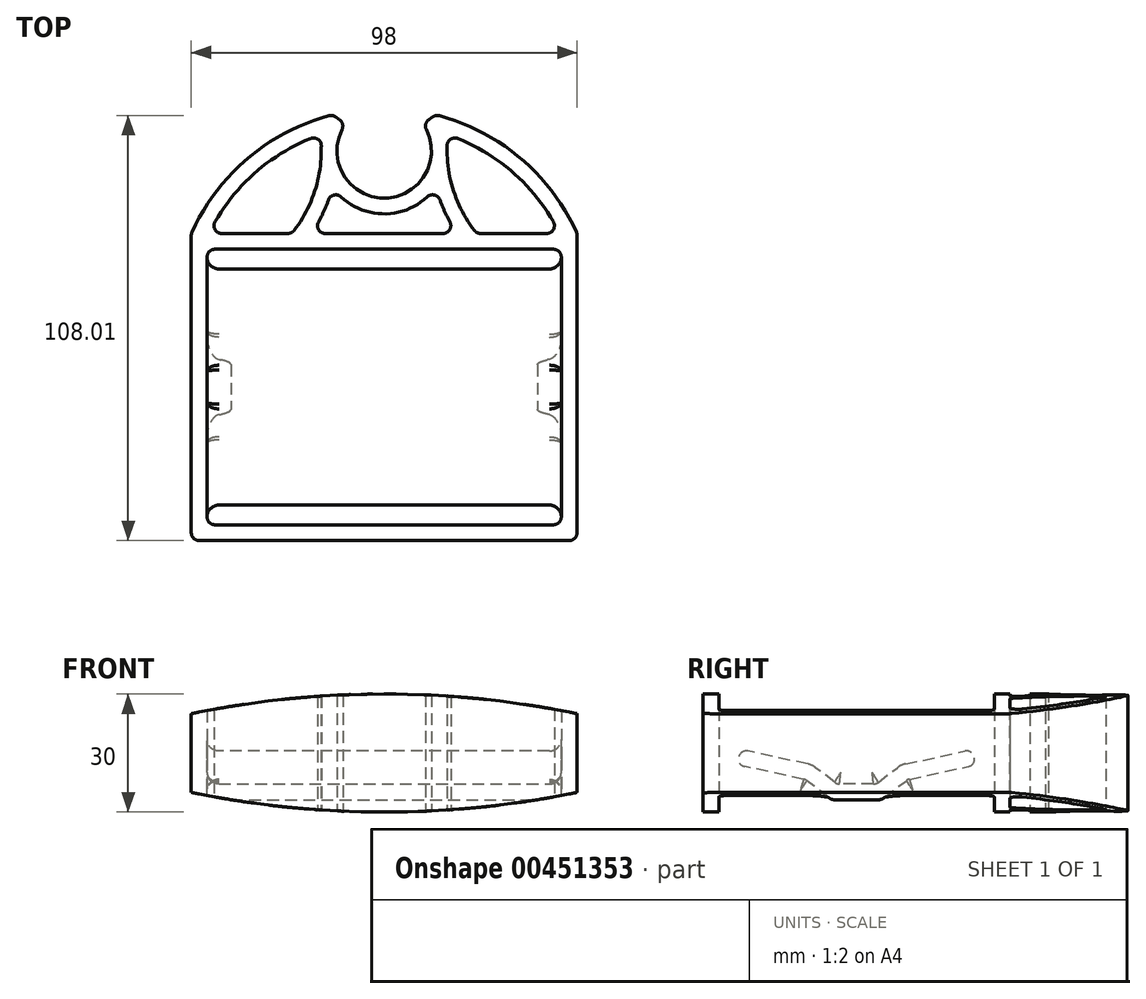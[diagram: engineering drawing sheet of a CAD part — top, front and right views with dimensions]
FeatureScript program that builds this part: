
annotation { "Feature Type Name" : "Feature", "Feature Type Description" : "" }
export const myFeature = defineFeature(function(context is Context, id is Id, definition is map)
    precondition{}
    {
        {
            var Q0;
            Q0=qCreatedBy(makeId("Top.planeOp"),FACE);
            var sketch = newSketch(context, id + "F0", { "sketchPlane" : qUnion([Q0])});
            skCircle(sketch, "E0", {"center": v(0, 0) * mm, "radius": 12 * mm});
            skSolve(sketch);
        }
        {
            var Q0;
            Q0=qCreatedBy(makeId("Top.planeOp"),FACE);
            var sketch = newSketch(context, id + "F1", { "sketchPlane" : qUnion([Q0])});
            skArc(sketch, "E1.0", {"start": v(-9.83, 6.88) * mm, "mid": v(-10.64, -5.54) * mm, "end": v(0, -12) * mm});
            skArc(sketch, "E2.0", {"start": v(-15.4, 4.36) * mm, "mid": v(-15.85, 2.2) * mm, "end": v(-16, 0) * mm});
            skLineSegment(sketch, "E3", {"start": v(0, -16) * mm, "end": v(0, -12) * mm});
            skLineSegment(sketch, "E4", {"start": v(0, 0) * mm, "end": v(0, -12) * mm, "construction": true});
            skPoint(sketch, "E5.orphan", {"position": v(0, 16) * mm});
            skLineSegment(sketch, "E6", {"start": v(-13.1, 9.18) * mm, "end": v(-9.83, 6.88) * mm});
            skLineSegment(sketch, "E7", {"start": v(0, 0) * mm, "end": v(-9.83, 6.88) * mm, "construction": true});
            skLineSegment(sketch, "E8", {"start": v(0, -16) * mm, "end": v(0, -21) * mm, "construction": true});
            skLineSegment(sketch, "E9", {"start": v(0, -21) * mm, "end": v(0, -25) * mm});
            skLineSegment(sketch, "E10", {"start": v(0, -21) * mm, "end": v(-18.54, -21) * mm});
            skLineSegment(sketch, "E11", {"start": v(0, -25) * mm, "end": v(-45, -25) * mm});
            skLineSegment(sketch, "E12", {"start": v(-49, -21) * mm, "end": v(-49, -99) * mm});
            skLineSegment(sketch, "E13", {"start": v(-45, -25) * mm, "end": v(-45, -95) * mm});
            skLineSegment(sketch, "E14", {"start": v(-45, -25) * mm, "end": v(-49, -25) * mm, "construction": true});
            skLineSegment(sketch, "E15", {"start": v(-45, -95) * mm, "end": v(0, -95) * mm});
            skLineSegment(sketch, "E16", {"start": v(0, -95) * mm, "end": v(0, -99) * mm});
            skLineSegment(sketch, "E17", {"start": v(0, -99) * mm, "end": v(-49, -99) * mm});
            skLineSegment(sketch, "E18", {"start": v(0, -25) * mm, "end": v(45, -25) * mm, "construction": true});
            skLineSegment(sketch, "E19", {"start": v(0, 0) * mm, "end": v(-12, 0) * mm, "construction": true});
            skArc(sketch, "E20", {"start": v(-13.1, 9.18) * mm, "mid": v(-34.52, -1.78) * mm, "end": v(-49, -21) * mm});
            skArc(sketch, "E21", {"start": v(-23.54, -21) * mm, "mid": v(-17.94, -11.16) * mm, "end": v(-16, 0) * mm});
            skArc(sketch, "E22", {"start": v(-18.54, -21) * mm, "mid": v(-15.31, -15.3) * mm, "end": v(-13.14, -9.12) * mm});
            skLineSegment(sketch, "E23", {"start": v(-17.94, -11.16) * mm, "end": v(-14.18, -12.5) * mm, "construction": true});
            skArc(sketch, "E24", {"start": v(-15.4, 4.36) * mm, "mid": v(-32.56, -5.36) * mm, "end": v(-44.58, -21) * mm});
            skLineSegment(sketch, "E25", {"start": v(-34.52, -1.78) * mm, "end": v(-31.95, -4.84) * mm, "construction": true});
            skArc(sketch, "E26.trimOffspring", {"start": v(-13.14, -9.12) * mm, "mid": v(-7.42, -14.18) * mm, "end": v(0, -16) * mm});
            skLineSegment(sketch, "E27.trimOffspring", {"start": v(-23.54, -21) * mm, "end": v(-44.58, -21) * mm});
            skSolve(sketch);
        }
        {
            var Q0;
            Q0 = qSketchRegion(id + "F1", true);
            extrude(context, id + "F2", {"entities" : qUnion([Q0]), "depth" : 30 * mm});
        }
        {
            var Q0;
            Q0=qCreatedBy(makeId("Right.planeOp"),FACE);
            var sketch = newSketch(context, id + "F3", { "sketchPlane" : qUnion([Q0])});
            skLineSegment(sketch, "E28", {"start": v(-95, 0) * mm, "end": v(-25, 0) * mm, "construction": true});
            skLineSegment(sketch, "E29", {"start": v(-60, 0) * mm, "end": v(-60, 30) * mm, "construction": true});
            skLineSegment(sketch, "E30", {"start": v(-95, 17.08) * mm, "end": v(-71.27, 11.98) * mm});
            skLineSegment(sketch, "E31", {"start": v(-71.27, 11.98) * mm, "end": v(-65, 7.14) * mm});
            skLineSegment(sketch, "E32.0", {"start": v(-73, 8.26) * mm, "end": v(-66.36, 3.14) * mm});
            skLineSegment(sketch, "E32.1", {"start": v(-95, 13) * mm, "end": v(-73, 8.26) * mm});
            skLineSegment(sketch, "E33", {"start": v(-95, 13) * mm, "end": v(-95, 17.08) * mm});
            skLineSegment(sketch, "E34.MirrorCS", {"start": v(-25, 13) * mm, "end": v(-47, 8.26) * mm});
            skLineSegment(sketch, "E35.MirrorCS", {"start": v(-25, 13) * mm, "end": v(-25, 17.08) * mm});
            skLineSegment(sketch, "E36.MirrorCS", {"start": v(-25, 17.08) * mm, "end": v(-48.73, 11.98) * mm});
            skLineSegment(sketch, "E37.MirrorCS", {"start": v(-48.73, 11.98) * mm, "end": v(-55, 7.14) * mm});
            skLineSegment(sketch, "E38.MirrorCS", {"start": v(-47, 8.26) * mm, "end": v(-53.64, 3.14) * mm});
            skLineSegment(sketch, "E39", {"start": v(-65, 7.14) * mm, "end": v(-55, 7.14) * mm});
            skLineSegment(sketch, "E40", {"start": v(-66.36, 3.14) * mm, "end": v(-53.64, 3.14) * mm});
            skLineSegment(sketch, "E41", {"start": v(-65, 7.14) * mm, "end": v(-65, 3.14) * mm, "construction": true});
            skSolve(sketch);
        }
        {
            var Q0;
            Q0 = qSketchRegion(id + "F3", true);
            extrude(context, id + "F4", {"entities" : qUnion([Q0]), "operationType" : NewBodyOperationType.ADD, "endBound" : BoundingType.UP_TO_NEXT, "oppositeDirection" : true, "depth" : 25 * mm});
        }
        {
            var Q0;
            Q0=qCreatedBy(makeId("Top.planeOp"),FACE);
            var sketch = newSketch(context, id + "F5", { "sketchPlane" : qUnion([Q0])});
            skLineSegment(sketch, "E42.bottom", {"start": v(-45, -25) * mm, "end": v(0, -25) * mm});
            skLineSegment(sketch, "E42.top", {"start": v(-45, -30) * mm, "end": v(0, -30) * mm});
            skLineSegment(sketch, "E42.left", {"start": v(-45, -25) * mm, "end": v(-45, -30) * mm});
            skLineSegment(sketch, "E42.right", {"start": v(0, -25) * mm, "end": v(0, -30) * mm});
            skLineSegment(sketch, "E43.bottom", {"start": v(-45, -95) * mm, "end": v(0, -95) * mm});
            skLineSegment(sketch, "E43.top", {"start": v(-45, -90) * mm, "end": v(0, -90) * mm});
            skLineSegment(sketch, "E43.left", {"start": v(-45, -95) * mm, "end": v(-45, -90) * mm});
            skLineSegment(sketch, "E43.right", {"start": v(0, -95) * mm, "end": v(0, -90) * mm});
            skSolve(sketch);
        }
        {
            var Q0;
            Q0 = qSketchRegion(id + "F5", true);
            extrude(context, id + "F6", {"entities" : qUnion([Q0]), "operationType" : NewBodyOperationType.REMOVE, "endBound" : BoundingType.THROUGH_ALL, "depth" : 25 * mm});
        }
        {
            var Q0;
            Q0=makeQuery(id+"F2.opExtrude","SWEPT_EDGE",EDGE,{"disambiguationData":[OSD([sQuery(id+"F1.wireOp",EDGE,"E11"),sQuery(id+"F1.wireOp",EDGE,"E13")])]});
            var Q1;
            Q1=makeQuery(id+"F2.opExtrude","SWEPT_EDGE",EDGE,{"disambiguationData":[OSD([sQuery(id+"F1.wireOp",EDGE,"E13"),sQuery(id+"F1.wireOp",EDGE,"E15")])]});
            var Q2;
            Q2=makeQuery(id+"F2.opExtrude","SWEPT_EDGE",EDGE,{"disambiguationData":[OSD([sQuery(id+"F1.wireOp",EDGE,"E6"),sQuery(id+"F1.wireOp",EDGE,"E20")])]});
            var Q3;
            Q3=makeQuery(id+"F2.opExtrude","SWEPT_EDGE",EDGE,{"disambiguationData":[OSD([sQuery(id+"F1.wireOp",EDGE,"E1.0"),sQuery(id+"F1.wireOp",EDGE,"E6")])]});
            var Q4;
            Q4=makeQuery(id+"F2.opExtrude","SWEPT_EDGE",EDGE,{"disambiguationData":[OSD([sQuery(id+"F1.wireOp",EDGE,"E12"),sQuery(id+"F1.wireOp",EDGE,"E20")])]});
            var Q5;
            Q5=makeQuery(id+"F2.opExtrude","SWEPT_EDGE",EDGE,{"disambiguationData":[OSD([sQuery(id+"F1.wireOp",EDGE,"E12"),sQuery(id+"F1.wireOp",EDGE,"E17")])]});
            var Q6;
            Q6=makeQuery(id+"F2.opExtrude","SWEPT_EDGE",EDGE,{"disambiguationData":[OSD([sQuery(id+"F1.wireOp",EDGE,"E21"),sQuery(id+"F1.wireOp",EDGE,"E27.trimOffspring")])]});
            var Q7;
            Q7=makeQuery(id+"F2.opExtrude","SWEPT_EDGE",EDGE,{"disambiguationData":[OSD([sQuery(id+"F1.wireOp",EDGE,"E2.0"),sQuery(id+"F1.wireOp",EDGE,"E24")])]});
            var Q8;
            Q8=makeQuery(id+"F2.opExtrude","SWEPT_EDGE",EDGE,{"disambiguationData":[OSD([sQuery(id+"F1.wireOp",EDGE,"E22"),sQuery(id+"F1.wireOp",EDGE,"E26.trimOffspring")])]});
            var Q9;
            Q9=makeQuery(id+"F2.opExtrude","SWEPT_EDGE",EDGE,{"disambiguationData":[OSD([sQuery(id+"F1.wireOp",EDGE,"E10"),sQuery(id+"F1.wireOp",EDGE,"E22")])]});
            var Q10;
            Q10=makeQuery(id+"F2.opExtrude","SWEPT_EDGE",EDGE,{"disambiguationData":[OSD([sQuery(id+"F1.wireOp",EDGE,"E24"),sQuery(id+"F1.wireOp",EDGE,"E27.trimOffspring")])]});
            fillet(context, id + "F7", {"entities" : qUnion([Q0, Q1, Q2, Q3, Q4, Q5, Q6, Q7, Q8, Q9, Q10]), "radius" : 2 * mm, "tangentPropagation" : true, "allowEdgeOverflow" : false});
        }
        {
            var Q0;
            Q0=makeQuery(id+"F4.opExtrude","SWEPT_EDGE",EDGE,{"disambiguationData":[OSD([sQuery(id+"F3.wireOp",EDGE,"E36.MirrorCS"),sQuery(id+"F3.wireOp",EDGE,"E37.MirrorCS")])]});
            var Q1;
            Q1=makeQuery(id+"F4.opExtrude","SWEPT_EDGE",EDGE,{"disambiguationData":[OSD([sQuery(id+"F3.wireOp",EDGE,"E30"),sQuery(id+"F3.wireOp",EDGE,"E31")])]});
            fillet(context, id + "F8", {"entities" : qUnion([Q0, Q1]), "radius" : 5 * mm, "tangentPropagation" : true, "allowEdgeOverflow" : false});
        }
        {
            var Q0;
            Q0=makeQuery(id+"F4.opExtrude","SWEPT_EDGE",EDGE,{"disambiguationData":[OSD([sQuery(id+"F3.wireOp",EDGE,"E32.0"),sQuery(id+"F3.wireOp",EDGE,"E32.1")])]});
            fillet(context, id + "F9", {"entities" : qUnion([Q0]), "radius" : 2 * mm, "tangentPropagation" : true, "allowEdgeOverflow" : false});
        }
        {
            var Q0;
            Q0=makeQuery(id+"F4.opExtrude","SWEPT_EDGE",EDGE,{"disambiguationData":[OSD([sQuery(id+"F3.wireOp",EDGE,"E34.MirrorCS"),sQuery(id+"F3.wireOp",EDGE,"E38.MirrorCS")])]});
            var Q1;
            Q1=makeQuery(id+"F4.opExtrude","SWEPT_EDGE",EDGE,{"disambiguationData":[OSD([sQuery(id+"F3.wireOp",EDGE,"E32.0"),sQuery(id+"F3.wireOp",EDGE,"IAGzdYc4-z68C-EQy4-V6Kw-QF0httY63qSp")])]});
            var Q2;
            Q2=makeQuery(id+"F4.opExtrude","SWEPT_EDGE",EDGE,{"disambiguationData":[OSD([sQuery(id+"F3.wireOp",EDGE,"E31"),sQuery(id+"F3.wireOp",EDGE,"IAGzdYc4-z68C-EQy4-V6Kw-QF0httY63qSp")])]});
            var Q3;
            Q3=makeQuery(id+"F4.opExtrude","SWEPT_EDGE",EDGE,{"disambiguationData":[OSD([sQuery(id+"F3.wireOp",EDGE,"E38.MirrorCS"),sQuery(id+"F3.wireOp",EDGE,"90d33c85-e0a6-49d1-bc45-df9b89ce86660.MirrorCS")])]});
            var Q4;
            Q4=makeQuery(id+"F4.opExtrude","SWEPT_EDGE",EDGE,{"disambiguationData":[OSD([sQuery(id+"F3.wireOp",EDGE,"E37.MirrorCS"),sQuery(id+"F3.wireOp",EDGE,"90d33c85-e0a6-49d1-bc45-df9b89ce86660.MirrorCS")])]});
            var Q5;
            Q5=makeQuery(id+"F6.boolean.opBoolean","INTERSECT",EDGE,{"derivedFrom":[makeQuery(id+"F4.opExtrude","SWEPT_FACE",FACE,{"disambiguationData":[OSD([sQuery(id+"F3.wireOp",EDGE,"E30")])]}),makeQuery(id+"F6.opExtrude","SWEPT_FACE",FACE,{"disambiguationData":[OSD([sQuery(id+"F5.wireOp",EDGE,"E43.top")])]})]});
            var Q6;
            Q6=makeQuery(id+"F6.boolean.opBoolean","INTERSECT",EDGE,{"derivedFrom":[makeQuery(id+"F4.opExtrude","SWEPT_FACE",FACE,{"disambiguationData":[OSD([sQuery(id+"F3.wireOp",EDGE,"E32.1")])]}),makeQuery(id+"F6.opExtrude","SWEPT_FACE",FACE,{"disambiguationData":[OSD([sQuery(id+"F5.wireOp",EDGE,"E43.top")])]})]});
            var Q7;
            Q7=makeQuery(id+"F6.boolean.opBoolean","INTERSECT",EDGE,{"derivedFrom":[makeQuery(id+"F4.opExtrude","SWEPT_FACE",FACE,{"disambiguationData":[OSD([sQuery(id+"F3.wireOp",EDGE,"E36.MirrorCS")])]}),makeQuery(id+"F6.opExtrude","SWEPT_FACE",FACE,{"disambiguationData":[OSD([sQuery(id+"F5.wireOp",EDGE,"E42.top")])]})]});
            var Q8;
            Q8=makeQuery(id+"F6.boolean.opBoolean","INTERSECT",EDGE,{"derivedFrom":[makeQuery(id+"F4.opExtrude","SWEPT_FACE",FACE,{"disambiguationData":[OSD([sQuery(id+"F3.wireOp",EDGE,"E34.MirrorCS")])]}),makeQuery(id+"F6.opExtrude","SWEPT_FACE",FACE,{"disambiguationData":[OSD([sQuery(id+"F5.wireOp",EDGE,"E42.top")])]})]});
            fillet(context, id + "F10", {"entities" : qUnion([Q0, Q1, Q2, Q3, Q4, Q5, Q6, Q7, Q8]), "radius" : 2 * mm, "tangentPropagation" : true, "allowEdgeOverflow" : false});
        }
        {
            var Q0;
            Q0=makeQuery(id+"F4.opExtrude","SWEPT_EDGE",EDGE,{"disambiguationData":[OSD([sQuery(id+"F3.wireOp",EDGE,"E35.MirrorCS"),sQuery(id+"F3.wireOp",EDGE,"E36.MirrorCS")])]});
            var Q1;
            Q1=makeQuery(id+"F4.opExtrude","TWEAK_EDGE",EDGE,{"derivedFrom":[makeQuery(id+"F2.opExtrude","SWEPT_FACE",FACE,{"disambiguationData":[OSD([sQuery(id+"F1.wireOp",EDGE,"E13")])]}),makeQuery(id+"F3.imprint","IMPRINT",EDGE,{"derivedFrom":sQuery(id+"F3.wireOp",EDGE,"E30")})]});
            var Q2;
            Q2=makeQuery(id+"F10.opFillet","BLEND_EDGE",EDGE,{"blendedFrom":[makeQuery(id+"F4.opExtrude","SWEPT_EDGE",EDGE,{"disambiguationData":[OSD([sQuery(id+"F3.wireOp",EDGE,"E38.MirrorCS"),sQuery(id+"F3.wireOp",EDGE,"90d33c85-e0a6-49d1-bc45-df9b89ce86660.MirrorCS")])]}),makeQuery(id+"F6.boolean.opBoolean","MERGE",FACE,{"derivedFrom":[makeQuery(id+"F2.opExtrude","SWEPT_FACE",FACE,{"disambiguationData":[OSD([sQuery(id+"F1.wireOp",EDGE,"E13")])]}),makeQuery(id+"F6.opExtrude","SWEPT_FACE",FACE,{"disambiguationData":[OSD([sQuery(id+"F5.wireOp",EDGE,"E42.left")])]}),makeQuery(id+"F6.opExtrude","SWEPT_FACE",FACE,{"disambiguationData":[OSD([sQuery(id+"F5.wireOp",EDGE,"E43.left")])]})]})],"blendedInto":[makeQuery(id+"F6.boolean.opBoolean","MERGE",FACE,{"derivedFrom":[makeQuery(id+"F2.opExtrude","SWEPT_FACE",FACE,{"disambiguationData":[OSD([sQuery(id+"F1.wireOp",EDGE,"E13")])]}),makeQuery(id+"F6.opExtrude","SWEPT_FACE",FACE,{"disambiguationData":[OSD([sQuery(id+"F5.wireOp",EDGE,"E42.left")])]}),makeQuery(id+"F6.opExtrude","SWEPT_FACE",FACE,{"disambiguationData":[OSD([sQuery(id+"F5.wireOp",EDGE,"E43.left")])]})]})]});
            fillet(context, id + "F11", {"entities" : qUnion([Q0, Q1, Q2]), "radius" : 3 * mm, "tangentPropagation" : true, "allowEdgeOverflow" : false});
        }
        {
            var Q0;
            Q0=makeQuery(id+"F2.opExtrude","SWEPT_FACE",FACE,{"disambiguationData":[OSD([sQuery(id+"F1.wireOp",EDGE,"E17")])]});
            var sketch = newSketch(context, id + "F12", { "sketchPlane" : qUnion([Q0])});
            skArc(sketch, "E44", {"start": v(0, 30) * mm, "mid": v(-24.63, 28.75) * mm, "end": v(-49, 25) * mm});
            skLineSegment(sketch, "E45", {"start": v(0, 30) * mm, "end": v(-49, 30) * mm});
            skLineSegment(sketch, "E46", {"start": v(-49, 25) * mm, "end": v(-49, 30) * mm});
            skLineSegment(sketch, "E47", {"start": v(0, 15) * mm, "end": v(-50.15, 15) * mm, "construction": true});
            skArc(sketch, "E48.MirrorCS", {"start": v(0, 0) * mm, "mid": v(-24.63, 1.25) * mm, "end": v(-49, 5) * mm});
            skLineSegment(sketch, "E49.MirrorCS", {"start": v(-49, 5) * mm, "end": v(-49, 0) * mm});
            skLineSegment(sketch, "E50.MirrorCS", {"start": v(0, 0) * mm, "end": v(-49, 0) * mm});
            skSolve(sketch);
        }
        {
            var Q0;
            Q0 = qSketchRegion(id + "F12", true);
            extrude(context, id + "F13", {"entities" : qUnion([Q0]), "operationType" : NewBodyOperationType.REMOVE, "endBound" : BoundingType.THROUGH_ALL, "oppositeDirection" : true, "depth" : 25 * mm});
        }
        {
            var Q0;
            Q0=makeQuery(id+"F2.opExtrude","SWEPT_BODY",BODY,{"disambiguationData":[OSD([sQuery(id+"F1.wireOp",EDGE,"E1.0"),sQuery(id+"F1.wireOp",EDGE,"E2.0"),sQuery(id+"F1.wireOp",EDGE,"E3"),sQuery(id+"F1.wireOp",EDGE,"E6"),sQuery(id+"F1.wireOp",EDGE,"E9"),sQuery(id+"F1.wireOp",EDGE,"E10"),sQuery(id+"F1.wireOp",EDGE,"E11"),sQuery(id+"F1.wireOp",EDGE,"E12"),sQuery(id+"F1.wireOp",EDGE,"E13"),sQuery(id+"F1.wireOp",EDGE,"E15"),sQuery(id+"F1.wireOp",EDGE,"E16"),sQuery(id+"F1.wireOp",EDGE,"E17"),sQuery(id+"F1.wireOp",EDGE,"E20"),sQuery(id+"F1.wireOp",EDGE,"E21"),sQuery(id+"F1.wireOp",EDGE,"E22"),sQuery(id+"F1.wireOp",EDGE,"E24"),sQuery(id+"F1.wireOp",EDGE,"E26.trimOffspring"),sQuery(id+"F1.wireOp",EDGE,"E27.trimOffspring")])]});
            var Q1;
            Q1=qCreatedBy(makeId("Right.planeOp"),FACE);
            mirror(context, id + "F14", {"operationType" : NewBodyOperationType.ADD, "entities" : qUnion([Q0]), "mirrorPlane" : qUnion([Q1])});
        }
    });
